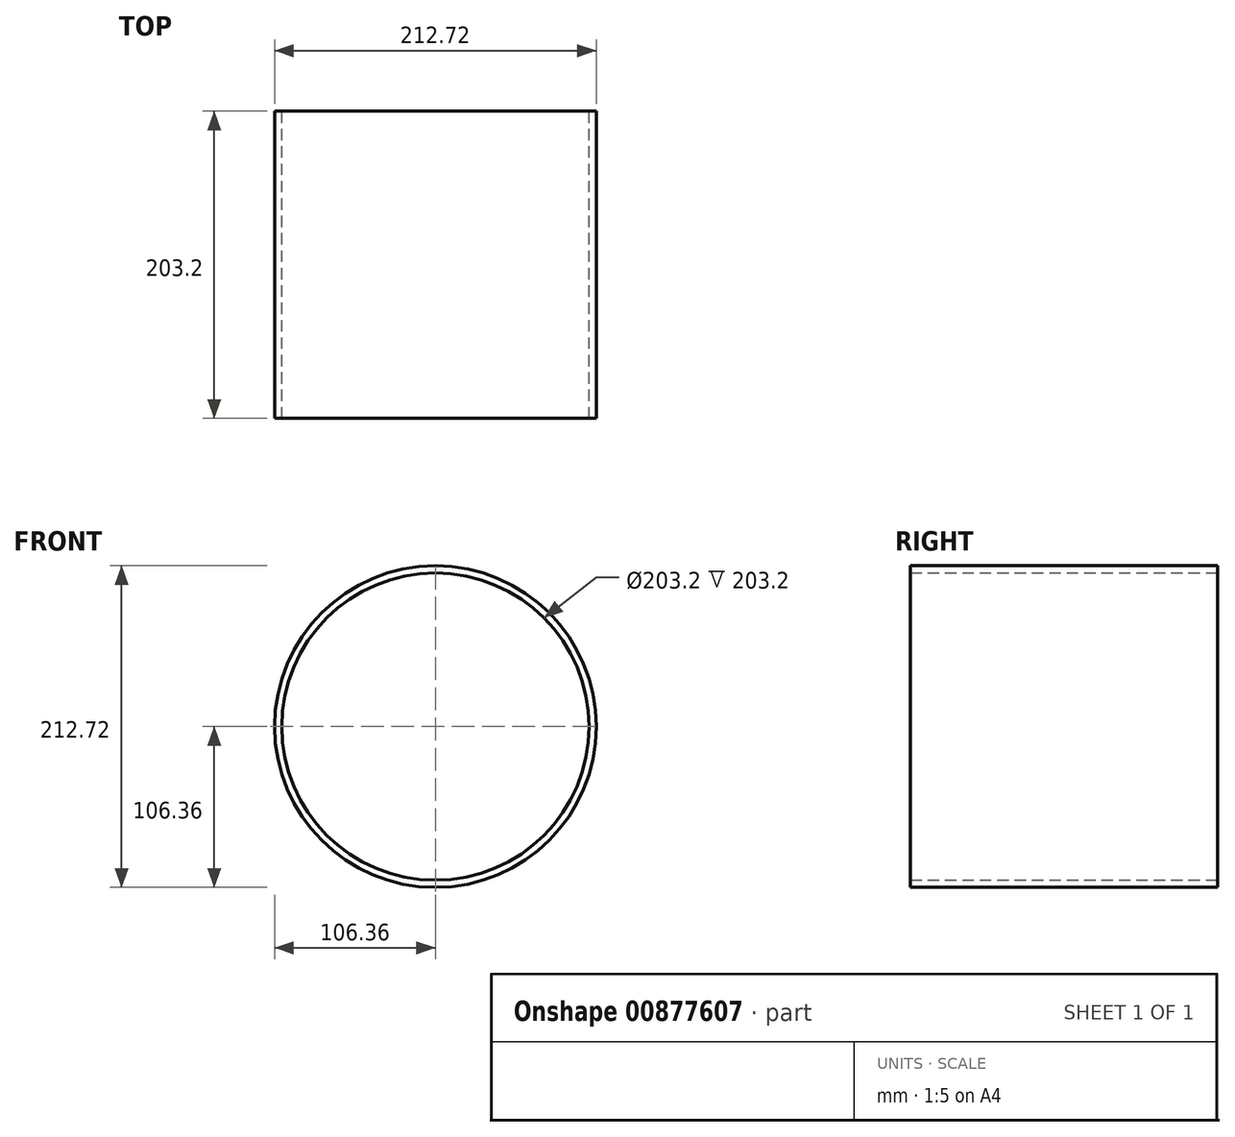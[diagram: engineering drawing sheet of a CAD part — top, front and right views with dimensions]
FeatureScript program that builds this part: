
annotation { "Feature Type Name" : "Feature", "Feature Type Description" : "" }
export const myFeature = defineFeature(function(context is Context, id is Id, definition is map)
    precondition{}
    {
        {
            var Q0;
            Q0=qCreatedBy(makeId("Front.planeOp"),FACE);
            var sketch = newSketch(context, id + "F0", { "sketchPlane" : qUnion([Q0])});
            skCircle(sketch, "E0", {"center": v(0, 0) * mm, "radius": 101.6 * mm});
            skCircle(sketch, "E1.0", {"center": v(0, 0) * mm, "radius": 106.36 * mm});
            skSolve(sketch);
        }
        {
            var Q0;
            Q0=makeQuery(id+"F0.imprint","IMPRINT",FACE,{"disambiguationData":[TD([[makeQuery(id+"F0.imprint","IMPRINT",EDGE,{"derivedFrom":sQuery(id+"F0.wireOp",EDGE,"E0")}),-1.0]])]});
            extrude(context, id + "F1", {"entities" : qUnion([Q0]), "depth" : 101.6 * mm, "offsetDistance" : 25.4 * mm, "hasSecondDirection" : true, "secondDirectionOppositeDirection" : true, "secondDirectionDepth" : 101.6 * mm});
        }
    });
